# Revit family: W-Wide-Flange-Column_Isolatek
name_source: partatom
category: Structural Columns
units: mm (PartAtom-declared; Revit-internal decimal feet)

## family parameters
Always export as geometry = No
Beam cutback in plan = From bounding box
Classification Number = 23.25.30.11.14.11
Cut with Voids When Loaded = No
Material for Model Behavior = Steel
Section Shape = Not Defined
Shared = No
Show family pre-cut in plan views = Yes

## types (1)
- W10X33
    A = 10.08 in²
    Assembly Code = D40
    Building Codes = http://www.cafco.com
    Fireproofing Material = <By Category>
    Installation-Fabrication = http://www.cafco.com
    Keynote = 07 81 23
    Manufacturer Fax = 973.347.9170
    Manufacturer Website = www.cafco.com
    Model = Wide Flange Steel Column with Fireproofing as Specified
    OmniClass Number = 23-13.25.11
    OmniClass Title = Fireproofing
    Product Data = http://www.cafco.com
    Revision = R#_02-2018
    Specification = http://www.cafco.com
    Test Data = http://www.cafco.com
    URL = http://www.arcat.com
    W = 33
    bf = 0' - 7 15/16"
    d = 0' - 9 3/4"
    k = 0' - 1 1/8"
    kr = 0' - 0 11/16"
    tf = 0' - 0 7/16"
    tw = 0' - 0 5/16"

## geometry (parser evidence)
native form markers: Blend x4, Sweep x1
no freeform markers — native parametric forms only
